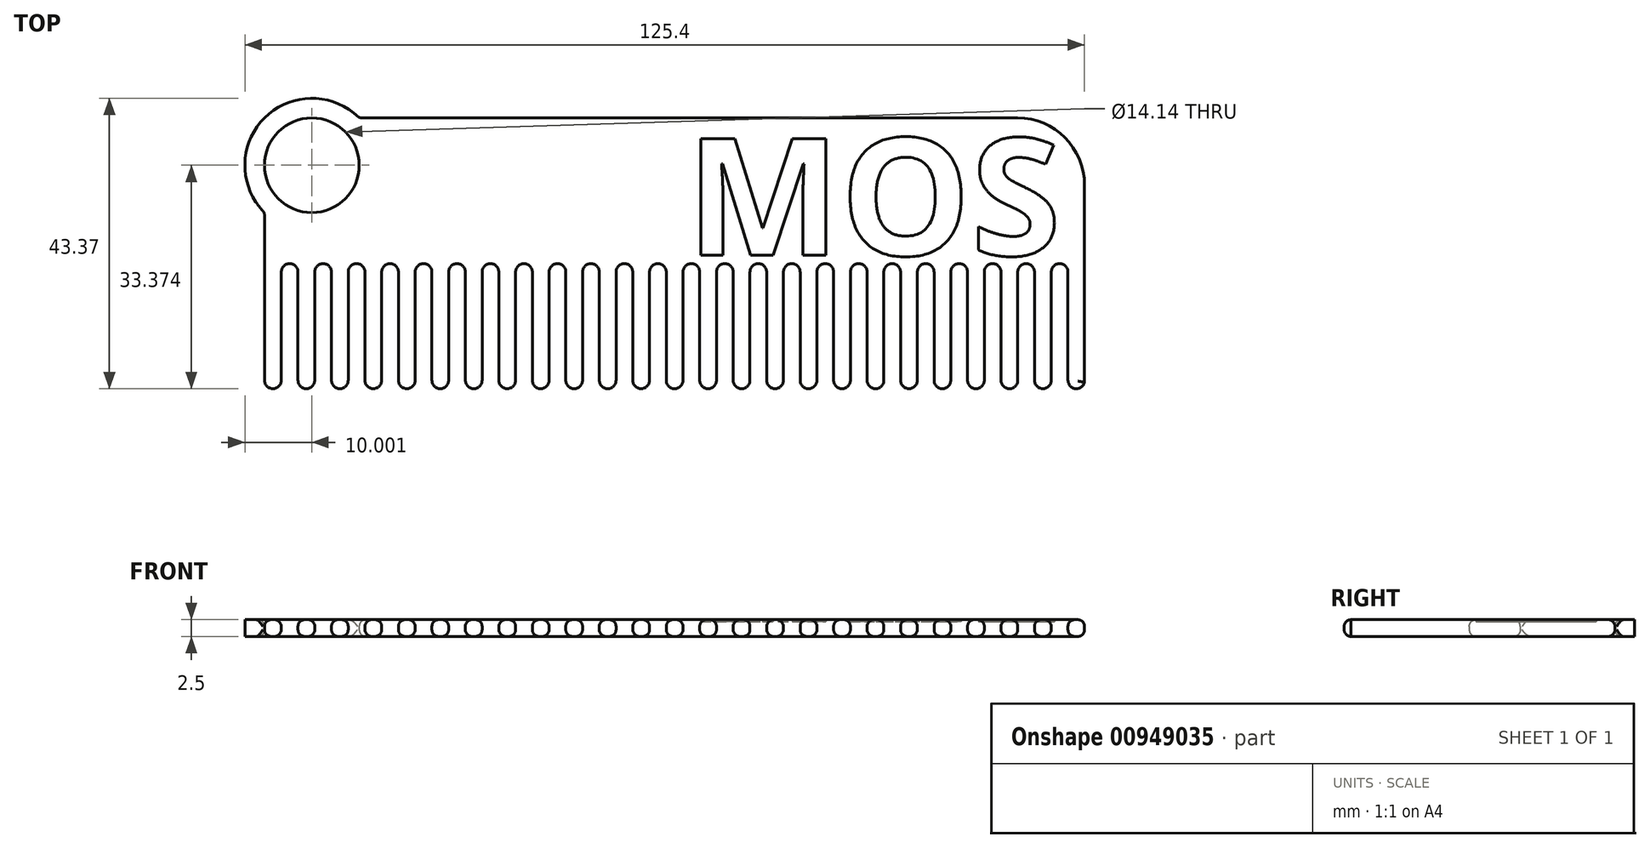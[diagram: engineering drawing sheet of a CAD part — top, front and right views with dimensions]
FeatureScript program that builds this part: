
annotation { "Feature Type Name" : "Feature", "Feature Type Description" : "" }
export const myFeature = defineFeature(function(context is Context, id is Id, definition is map)
    precondition{}
    {
        {
            var Q0;
            Q0=qCreatedBy(makeId("Top.planeOp"),FACE);
            var sketch = newSketch(context, id + "F0", { "sketchPlane" : qUnion([Q0])});
            skLineSegment(sketch, "E0.top", {"start": v(49.47, 20.52) * mm, "end": v(-63, 20.52) * mm});
            skLineSegment(sketch, "E0.left", {"start": v(59.47, -18.94) * mm, "end": v(59.47, 10.52) * mm});
            skLineSegment(sketch, "E1", {"start": v(-63, 20.52) * mm, "end": v(-55.93, 13.44) * mm, "construction": true});
            skCircle(sketch, "E2", {"center": v(-55.93, 13.44) * mm, "radius": 7.07 * mm});
            skCircle(sketch, "E3", {"center": v(-55.93, 13.44) * mm, "radius": 10 * mm});
            skPoint(sketch, "E4.visualSharp", {"position": v(59.47, 20.52) * mm});
            skArc(sketch, "E4.filletArc", {"start": v(59.47, 10.52) * mm, "mid": v(56.54, 17.59) * mm, "end": v(49.47, 20.52) * mm});
            skLineSegment(sketch, "E5", {"start": v(-63, -18.68) * mm, "end": v(-63, 20.52) * mm});
            skPoint(sketch, "E6", {"position": v(-60.5, -19.93) * mm});
            skPoint(sketch, "E7.1.0.0", {"position": v(-58, -19.93) * mm});
            skPoint(sketch, "E7.2.0.0", {"position": v(-55.5, -19.93) * mm});
            skPoint(sketch, "E7.3.0.0", {"position": v(-53, -19.93) * mm});
            skPoint(sketch, "E7.4.0.0", {"position": v(-50.5, -19.93) * mm});
            skPoint(sketch, "E7.5.0.0", {"position": v(-48, -19.93) * mm});
            skPoint(sketch, "E7.6.0.0", {"position": v(-45.5, -19.93) * mm});
            skPoint(sketch, "E7.7.0.0", {"position": v(-43, -19.93) * mm});
            skPoint(sketch, "E7.8.0.0", {"position": v(-40.5, -19.93) * mm});
            skPoint(sketch, "E7.9.0.0", {"position": v(-38, -19.93) * mm});
            skPoint(sketch, "E7.10.0.0", {"position": v(-35.5, -19.93) * mm});
            skPoint(sketch, "E7.11.0.0", {"position": v(-33, -19.93) * mm});
            skPoint(sketch, "E7.12.0.0", {"position": v(-30.5, -19.93) * mm});
            skPoint(sketch, "E7.13.0.0", {"position": v(-28, -19.93) * mm});
            skPoint(sketch, "E7.14.0.0", {"position": v(-25.5, -19.93) * mm});
            skPoint(sketch, "E7.15.0.0", {"position": v(-23, -19.93) * mm});
            skPoint(sketch, "E7.16.0.0", {"position": v(-20.5, -19.93) * mm});
            skPoint(sketch, "E7.17.0.0", {"position": v(-18, -19.93) * mm});
            skPoint(sketch, "E7.18.0.0", {"position": v(-15.5, -19.93) * mm});
            skPoint(sketch, "E7.19.0.0", {"position": v(-13, -19.93) * mm});
            skPoint(sketch, "E7.20.0.0", {"position": v(-10.5, -19.93) * mm});
            skPoint(sketch, "E7.21.0.0", {"position": v(-8, -19.93) * mm});
            skPoint(sketch, "E7.22.0.0", {"position": v(-5.5, -19.93) * mm});
            skPoint(sketch, "E7.23.0.0", {"position": v(-3, -19.93) * mm});
            skPoint(sketch, "E7.24.0.0", {"position": v(-0.5, -19.93) * mm});
            skPoint(sketch, "E7.25.0.0", {"position": v(2, -19.93) * mm});
            skPoint(sketch, "E7.26.0.0", {"position": v(4.5, -19.93) * mm});
            skPoint(sketch, "E7.27.0.0", {"position": v(7, -19.93) * mm});
            skPoint(sketch, "E7.28.0.0", {"position": v(9.5, -19.93) * mm});
            skPoint(sketch, "E7.29.0.0", {"position": v(12, -19.93) * mm});
            skPoint(sketch, "E7.30.0.0", {"position": v(14.5, -19.93) * mm});
            skPoint(sketch, "E7.31.0.0", {"position": v(17, -19.93) * mm});
            skPoint(sketch, "E7.32.0.0", {"position": v(19.5, -19.93) * mm});
            skPoint(sketch, "E7.33.0.0", {"position": v(22, -19.93) * mm});
            skPoint(sketch, "E7.34.0.0", {"position": v(24.5, -19.93) * mm});
            skPoint(sketch, "E7.35.0.0", {"position": v(27, -19.93) * mm});
            skPoint(sketch, "E7.36.0.0", {"position": v(29.5, -19.93) * mm});
            skPoint(sketch, "E7.37.0.0", {"position": v(32, -19.93) * mm});
            skPoint(sketch, "E7.38.0.0", {"position": v(34.5, -19.93) * mm});
            skPoint(sketch, "E7.39.0.0", {"position": v(37, -19.93) * mm});
            skPoint(sketch, "E7.40.0.0", {"position": v(39.5, -19.93) * mm});
            skPoint(sketch, "E7.41.0.0", {"position": v(42, -19.93) * mm});
            skPoint(sketch, "E7.42.0.0", {"position": v(44.5, -19.93) * mm});
            skPoint(sketch, "E7.43.0.0", {"position": v(47, -19.93) * mm});
            skPoint(sketch, "E7.44.0.0", {"position": v(49.5, -19.93) * mm});
            skPoint(sketch, "E7.45.0.0", {"position": v(52, -19.93) * mm});
            skPoint(sketch, "E7.46.0.0", {"position": v(54.5, -19.93) * mm});
            skPoint(sketch, "E7.47.0.0", {"position": v(57, -19.93) * mm});
            skLineSegment(sketch, "E8", {"start": v(57, -1.25) * mm, "end": v(-63, -1.25) * mm, "construction": true});
            skPoint(sketch, "E9", {"position": v(-60.5, -1.25) * mm});
            skPoint(sketch, "E10.1.0.0", {"position": v(-58, -1.25) * mm});
            skPoint(sketch, "E10.2.0.0", {"position": v(-55.5, -1.25) * mm});
            skPoint(sketch, "E10.3.0.0", {"position": v(-53, -1.25) * mm});
            skPoint(sketch, "E10.4.0.0", {"position": v(-50.5, -1.25) * mm});
            skPoint(sketch, "E10.5.0.0", {"position": v(-48, -1.25) * mm});
            skPoint(sketch, "E10.6.0.0", {"position": v(-45.5, -1.25) * mm});
            skPoint(sketch, "E10.7.0.0", {"position": v(-43, -1.25) * mm});
            skPoint(sketch, "E10.8.0.0", {"position": v(-40.5, -1.25) * mm});
            skPoint(sketch, "E10.9.0.0", {"position": v(-38, -1.25) * mm});
            skPoint(sketch, "E10.10.0.0", {"position": v(-35.5, -1.25) * mm});
            skPoint(sketch, "E10.11.0.0", {"position": v(-33, -1.25) * mm});
            skPoint(sketch, "E10.12.0.0", {"position": v(-30.5, -1.25) * mm});
            skPoint(sketch, "E10.13.0.0", {"position": v(-28, -1.25) * mm});
            skPoint(sketch, "E10.14.0.0", {"position": v(-25.5, -1.25) * mm});
            skPoint(sketch, "E10.15.0.0", {"position": v(-23, -1.25) * mm});
            skPoint(sketch, "E10.16.0.0", {"position": v(-20.5, -1.25) * mm});
            skPoint(sketch, "E10.17.0.0", {"position": v(-18, -1.25) * mm});
            skPoint(sketch, "E10.18.0.0", {"position": v(-15.5, -1.25) * mm});
            skPoint(sketch, "E10.19.0.0", {"position": v(-13, -1.25) * mm});
            skPoint(sketch, "E10.20.0.0", {"position": v(-10.5, -1.25) * mm});
            skPoint(sketch, "E10.21.0.0", {"position": v(-8, -1.25) * mm});
            skPoint(sketch, "E10.22.0.0", {"position": v(-5.5, -1.25) * mm});
            skPoint(sketch, "E10.23.0.0", {"position": v(-3, -1.25) * mm});
            skPoint(sketch, "E10.24.0.0", {"position": v(-0.5, -1.25) * mm});
            skPoint(sketch, "E10.25.0.0", {"position": v(2, -1.25) * mm});
            skPoint(sketch, "E10.26.0.0", {"position": v(4.5, -1.25) * mm});
            skPoint(sketch, "E10.27.0.0", {"position": v(7, -1.25) * mm});
            skPoint(sketch, "E10.28.0.0", {"position": v(9.5, -1.25) * mm});
            skPoint(sketch, "E10.29.0.0", {"position": v(12, -1.25) * mm});
            skPoint(sketch, "E10.30.0.0", {"position": v(14.5, -1.25) * mm});
            skPoint(sketch, "E10.31.0.0", {"position": v(17, -1.25) * mm});
            skPoint(sketch, "E10.32.0.0", {"position": v(19.5, -1.25) * mm});
            skPoint(sketch, "E10.33.0.0", {"position": v(22, -1.25) * mm});
            skPoint(sketch, "E10.34.0.0", {"position": v(24.5, -1.25) * mm});
            skPoint(sketch, "E10.35.0.0", {"position": v(27, -1.25) * mm});
            skPoint(sketch, "E10.36.0.0", {"position": v(29.5, -1.25) * mm});
            skPoint(sketch, "E10.37.0.0", {"position": v(32, -1.25) * mm});
            skPoint(sketch, "E10.38.0.0", {"position": v(34.5, -1.25) * mm});
            skPoint(sketch, "E10.39.0.0", {"position": v(37, -1.25) * mm});
            skPoint(sketch, "E10.40.0.0", {"position": v(39.5, -1.25) * mm});
            skPoint(sketch, "E10.41.0.0", {"position": v(42, -1.25) * mm});
            skPoint(sketch, "E10.42.0.0", {"position": v(44.5, -1.25) * mm});
            skPoint(sketch, "E10.43.0.0", {"position": v(47, -1.25) * mm});
            skPoint(sketch, "E10.44.0.0", {"position": v(49.5, -1.25) * mm});
            skPoint(sketch, "E10.45.0.0", {"position": v(52, -1.25) * mm});
            skPoint(sketch, "E10.46.0.0", {"position": v(54.5, -1.25) * mm});
            skPoint(sketch, "E10.47.0.0", {"position": v(57, -1.25) * mm});
            skLineSegment(sketch, "E10.direction1", {"start": v(-60.5, -1.25) * mm, "end": v(-58, -1.25) * mm, "construction": true});
            skPoint(sketch, "E11.positionSnap0", {"position": v(-59.25, -1.25) * mm});
            skArc(sketch, "E12", {"start": v(-58, -2.5) * mm, "mid": v(-59.25, -1.25) * mm, "end": v(-60.5, -2.5) * mm});
            skArc(sketch, "E13.1.0.0", {"start": v(-53, -2.5) * mm, "mid": v(-54.25, -1.25) * mm, "end": v(-55.5, -2.5) * mm});
            skArc(sketch, "E13.2.0.0", {"start": v(-48, -2.5) * mm, "mid": v(-49.25, -1.25) * mm, "end": v(-50.5, -2.5) * mm});
            skArc(sketch, "E13.3.0.0", {"start": v(-43, -2.5) * mm, "mid": v(-44.25, -1.25) * mm, "end": v(-45.5, -2.5) * mm});
            skArc(sketch, "E13.4.0.0", {"start": v(-38, -2.5) * mm, "mid": v(-39.25, -1.25) * mm, "end": v(-40.5, -2.5) * mm});
            skArc(sketch, "E13.5.0.0", {"start": v(-33, -2.5) * mm, "mid": v(-34.25, -1.25) * mm, "end": v(-35.5, -2.5) * mm});
            skArc(sketch, "E13.6.0.0", {"start": v(-28, -2.5) * mm, "mid": v(-29.25, -1.25) * mm, "end": v(-30.5, -2.5) * mm});
            skArc(sketch, "E13.7.0.0", {"start": v(-23, -2.5) * mm, "mid": v(-24.25, -1.25) * mm, "end": v(-25.5, -2.5) * mm});
            skArc(sketch, "E13.8.0.0", {"start": v(-18, -2.5) * mm, "mid": v(-19.25, -1.25) * mm, "end": v(-20.5, -2.5) * mm});
            skArc(sketch, "E13.9.0.0", {"start": v(-13, -2.5) * mm, "mid": v(-14.25, -1.25) * mm, "end": v(-15.5, -2.5) * mm});
            skArc(sketch, "E13.10.0.0", {"start": v(-8, -2.5) * mm, "mid": v(-9.25, -1.25) * mm, "end": v(-10.5, -2.5) * mm});
            skArc(sketch, "E13.11.0.0", {"start": v(-3, -2.5) * mm, "mid": v(-4.25, -1.25) * mm, "end": v(-5.5, -2.5) * mm});
            skArc(sketch, "E13.12.0.0", {"start": v(2, -2.5) * mm, "mid": v(0.75, -1.25) * mm, "end": v(-0.5, -2.5) * mm});
            skArc(sketch, "E13.13.0.0", {"start": v(7, -2.5) * mm, "mid": v(5.75, -1.25) * mm, "end": v(4.5, -2.5) * mm});
            skArc(sketch, "E13.14.0.0", {"start": v(12, -2.5) * mm, "mid": v(10.75, -1.25) * mm, "end": v(9.5, -2.5) * mm});
            skArc(sketch, "E13.15.0.0", {"start": v(17, -2.5) * mm, "mid": v(15.75, -1.25) * mm, "end": v(14.5, -2.5) * mm});
            skArc(sketch, "E13.16.0.0", {"start": v(22, -2.5) * mm, "mid": v(20.75, -1.25) * mm, "end": v(19.5, -2.5) * mm});
            skArc(sketch, "E13.17.0.0", {"start": v(27, -2.5) * mm, "mid": v(25.75, -1.25) * mm, "end": v(24.5, -2.5) * mm});
            skArc(sketch, "E13.18.0.0", {"start": v(32, -2.5) * mm, "mid": v(30.75, -1.25) * mm, "end": v(29.5, -2.5) * mm});
            skArc(sketch, "E13.19.0.0", {"start": v(37, -2.5) * mm, "mid": v(35.75, -1.25) * mm, "end": v(34.5, -2.5) * mm});
            skArc(sketch, "E13.20.0.0", {"start": v(42, -2.5) * mm, "mid": v(40.75, -1.25) * mm, "end": v(39.5, -2.5) * mm});
            skArc(sketch, "E13.21.0.0", {"start": v(47, -2.5) * mm, "mid": v(45.75, -1.25) * mm, "end": v(44.5, -2.5) * mm});
            skArc(sketch, "E13.22.0.0", {"start": v(52, -2.5) * mm, "mid": v(50.75, -1.25) * mm, "end": v(49.5, -2.5) * mm});
            skArc(sketch, "E13.23.0.0", {"start": v(57, -2.5) * mm, "mid": v(55.75, -1.25) * mm, "end": v(54.5, -2.5) * mm});
            skLineSegment(sketch, "E13.direction1", {"start": v(-59.25, -2.5) * mm, "end": v(-54.25, -2.5) * mm, "construction": true});
            skPoint(sketch, "E14.0.48.0", {"position": v(59.5, -1.25) * mm});
            skPoint(sketch, "E15.0.48.0", {"position": v(59.5, -19.93) * mm});
            skLineSegment(sketch, "E16", {"start": v(57, -1.25) * mm, "end": v(59.5, -1.25) * mm, "construction": true});
            skArc(sketch, "E17", {"start": v(-63, -18.68) * mm, "mid": v(-61.75, -19.93) * mm, "end": v(-60.5, -18.68) * mm});
            skArc(sketch, "E18.1.0.0", {"start": v(-58, -18.68) * mm, "mid": v(-56.75, -19.93) * mm, "end": v(-55.5, -18.68) * mm});
            skArc(sketch, "E18.2.0.0", {"start": v(-53, -18.68) * mm, "mid": v(-51.75, -19.93) * mm, "end": v(-50.5, -18.68) * mm});
            skArc(sketch, "E18.3.0.0", {"start": v(-48, -18.68) * mm, "mid": v(-46.75, -19.93) * mm, "end": v(-45.5, -18.68) * mm});
            skArc(sketch, "E18.4.0.0", {"start": v(-43, -18.68) * mm, "mid": v(-41.75, -19.93) * mm, "end": v(-40.5, -18.68) * mm});
            skArc(sketch, "E18.5.0.0", {"start": v(-38, -18.68) * mm, "mid": v(-36.75, -19.93) * mm, "end": v(-35.5, -18.68) * mm});
            skArc(sketch, "E18.6.0.0", {"start": v(-33, -18.68) * mm, "mid": v(-31.75, -19.93) * mm, "end": v(-30.5, -18.68) * mm});
            skArc(sketch, "E18.7.0.0", {"start": v(-28, -18.68) * mm, "mid": v(-26.75, -19.93) * mm, "end": v(-25.5, -18.68) * mm});
            skArc(sketch, "E18.8.0.0", {"start": v(-23, -18.68) * mm, "mid": v(-21.75, -19.93) * mm, "end": v(-20.5, -18.68) * mm});
            skArc(sketch, "E18.9.0.0", {"start": v(-18, -18.68) * mm, "mid": v(-16.75, -19.93) * mm, "end": v(-15.5, -18.68) * mm});
            skArc(sketch, "E18.10.0.0", {"start": v(-13, -18.68) * mm, "mid": v(-11.75, -19.93) * mm, "end": v(-10.5, -18.68) * mm});
            skArc(sketch, "E18.11.0.0", {"start": v(-8, -18.68) * mm, "mid": v(-6.75, -19.93) * mm, "end": v(-5.5, -18.68) * mm});
            skArc(sketch, "E18.12.0.0", {"start": v(-3, -18.68) * mm, "mid": v(-1.75, -19.93) * mm, "end": v(-0.5, -18.68) * mm});
            skArc(sketch, "E18.13.0.0", {"start": v(2, -18.68) * mm, "mid": v(3.25, -19.93) * mm, "end": v(4.5, -18.68) * mm});
            skArc(sketch, "E18.14.0.0", {"start": v(7, -18.68) * mm, "mid": v(8.25, -19.93) * mm, "end": v(9.5, -18.68) * mm});
            skArc(sketch, "E18.15.0.0", {"start": v(12, -18.68) * mm, "mid": v(13.25, -19.93) * mm, "end": v(14.5, -18.68) * mm});
            skArc(sketch, "E18.16.0.0", {"start": v(17, -18.68) * mm, "mid": v(18.25, -19.93) * mm, "end": v(19.5, -18.68) * mm});
            skArc(sketch, "E18.17.0.0", {"start": v(22, -18.68) * mm, "mid": v(23.25, -19.93) * mm, "end": v(24.5, -18.68) * mm});
            skArc(sketch, "E18.18.0.0", {"start": v(27, -18.68) * mm, "mid": v(28.25, -19.93) * mm, "end": v(29.5, -18.68) * mm});
            skArc(sketch, "E18.19.0.0", {"start": v(32, -18.68) * mm, "mid": v(33.25, -19.93) * mm, "end": v(34.5, -18.68) * mm});
            skArc(sketch, "E18.20.0.0", {"start": v(37, -18.68) * mm, "mid": v(38.25, -19.93) * mm, "end": v(39.5, -18.68) * mm});
            skArc(sketch, "E18.21.0.0", {"start": v(42, -18.68) * mm, "mid": v(43.25, -19.93) * mm, "end": v(44.5, -18.68) * mm});
            skArc(sketch, "E18.22.0.0", {"start": v(47, -18.68) * mm, "mid": v(48.25, -19.93) * mm, "end": v(49.5, -18.68) * mm});
            skArc(sketch, "E18.23.0.0", {"start": v(52, -18.68) * mm, "mid": v(53.25, -19.93) * mm, "end": v(54.5, -18.68) * mm});
            skLineSegment(sketch, "E18.direction1", {"start": v(-61.75, -18.68) * mm, "end": v(-56.75, -18.68) * mm, "construction": true});
            skArc(sketch, "E19.0.24.0", {"start": v(57, -18.68) * mm, "mid": v(58.12, -19.92) * mm, "end": v(59.47, -18.94) * mm});
            skLineSegment(sketch, "E20", {"start": v(-60.5, -1.25) * mm, "end": v(-60.5, -18.68) * mm});
            skLineSegment(sketch, "E21.1.0.0", {"start": v(-58, -1.25) * mm, "end": v(-58, -19.93) * mm});
            skLineSegment(sketch, "E21.2.0.0", {"start": v(-55.5, -1.25) * mm, "end": v(-55.5, -19.93) * mm});
            skLineSegment(sketch, "E21.3.0.0", {"start": v(-53, -1.25) * mm, "end": v(-53, -18.68) * mm});
            skLineSegment(sketch, "E21.4.0.0", {"start": v(-50.5, -1.25) * mm, "end": v(-50.5, -18.68) * mm});
            skLineSegment(sketch, "E21.5.0.0", {"start": v(-48, -1.25) * mm, "end": v(-48, -18.68) * mm});
            skLineSegment(sketch, "E21.6.0.0", {"start": v(-45.5, -1.25) * mm, "end": v(-45.5, -19.93) * mm});
            skLineSegment(sketch, "E21.7.0.0", {"start": v(-43, -1.25) * mm, "end": v(-43, -18.68) * mm});
            skLineSegment(sketch, "E21.8.0.0", {"start": v(-40.5, -1.25) * mm, "end": v(-40.5, -18.68) * mm});
            skLineSegment(sketch, "E21.9.0.0", {"start": v(-38, -1.25) * mm, "end": v(-38, -18.68) * mm});
            skLineSegment(sketch, "E21.10.0.0", {"start": v(-35.5, -1.25) * mm, "end": v(-35.5, -18.68) * mm});
            skLineSegment(sketch, "E21.11.0.0", {"start": v(-33, -1.25) * mm, "end": v(-33, -18.68) * mm});
            skLineSegment(sketch, "E21.12.0.0", {"start": v(-30.5, -1.25) * mm, "end": v(-30.5, -19.93) * mm});
            skLineSegment(sketch, "E21.13.0.0", {"start": v(-28, -1.25) * mm, "end": v(-28, -18.68) * mm});
            skLineSegment(sketch, "E21.14.0.0", {"start": v(-25.5, -1.25) * mm, "end": v(-25.5, -18.68) * mm});
            skLineSegment(sketch, "E21.15.0.0", {"start": v(-23, -1.25) * mm, "end": v(-23, -18.68) * mm});
            skLineSegment(sketch, "E21.16.0.0", {"start": v(-20.5, -1.25) * mm, "end": v(-20.5, -18.68) * mm});
            skLineSegment(sketch, "E21.17.0.0", {"start": v(-18, -1.25) * mm, "end": v(-18, -18.68) * mm});
            skLineSegment(sketch, "E21.18.0.0", {"start": v(-15.5, -1.25) * mm, "end": v(-15.5, -18.68) * mm});
            skLineSegment(sketch, "E21.19.0.0", {"start": v(-13, -1.25) * mm, "end": v(-13, -18.68) * mm});
            skLineSegment(sketch, "E21.20.0.0", {"start": v(-10.5, -1.25) * mm, "end": v(-10.5, -18.68) * mm});
            skLineSegment(sketch, "E21.21.0.0", {"start": v(-8, -1.25) * mm, "end": v(-8, -18.68) * mm});
            skLineSegment(sketch, "E21.22.0.0", {"start": v(-5.5, -1.25) * mm, "end": v(-5.5, -18.68) * mm});
            skLineSegment(sketch, "E21.23.0.0", {"start": v(-3, -1.25) * mm, "end": v(-3, -18.68) * mm});
            skLineSegment(sketch, "E21.24.0.0", {"start": v(-0.5, -1.25) * mm, "end": v(-0.5, -18.68) * mm});
            skLineSegment(sketch, "E21.25.0.0", {"start": v(2, -1.25) * mm, "end": v(2, -18.68) * mm});
            skLineSegment(sketch, "E21.26.0.0", {"start": v(4.5, -1.25) * mm, "end": v(4.5, -18.68) * mm});
            skLineSegment(sketch, "E21.27.0.0", {"start": v(7, -1.25) * mm, "end": v(7, -18.68) * mm});
            skLineSegment(sketch, "E21.28.0.0", {"start": v(9.5, -1.25) * mm, "end": v(9.5, -18.68) * mm});
            skLineSegment(sketch, "E21.29.0.0", {"start": v(12, -1.25) * mm, "end": v(12, -18.68) * mm});
            skLineSegment(sketch, "E21.30.0.0", {"start": v(14.5, -1.25) * mm, "end": v(14.5, -18.68) * mm});
            skLineSegment(sketch, "E21.31.0.0", {"start": v(17, -1.25) * mm, "end": v(17, -18.68) * mm});
            skLineSegment(sketch, "E21.32.0.0", {"start": v(19.5, -1.25) * mm, "end": v(19.5, -18.68) * mm});
            skLineSegment(sketch, "E21.33.0.0", {"start": v(22, -1.25) * mm, "end": v(22, -18.68) * mm});
            skLineSegment(sketch, "E21.34.0.0", {"start": v(24.5, -1.25) * mm, "end": v(24.5, -18.68) * mm});
            skLineSegment(sketch, "E21.35.0.0", {"start": v(27, -1.25) * mm, "end": v(27, -18.68) * mm});
            skLineSegment(sketch, "E21.36.0.0", {"start": v(29.5, -1.25) * mm, "end": v(29.5, -18.68) * mm});
            skLineSegment(sketch, "E21.37.0.0", {"start": v(32, -1.25) * mm, "end": v(32, -18.68) * mm});
            skLineSegment(sketch, "E21.38.0.0", {"start": v(34.5, -1.25) * mm, "end": v(34.5, -18.68) * mm});
            skLineSegment(sketch, "E21.39.0.0", {"start": v(37, -1.25) * mm, "end": v(37, -18.68) * mm});
            skLineSegment(sketch, "E21.40.0.0", {"start": v(39.5, -1.25) * mm, "end": v(39.5, -18.68) * mm});
            skLineSegment(sketch, "E21.41.0.0", {"start": v(42, -1.25) * mm, "end": v(42, -18.68) * mm});
            skLineSegment(sketch, "E21.42.0.0", {"start": v(44.5, -1.25) * mm, "end": v(44.5, -18.68) * mm});
            skLineSegment(sketch, "E21.43.0.0", {"start": v(47, -1.25) * mm, "end": v(47, -18.68) * mm});
            skLineSegment(sketch, "E21.44.0.0", {"start": v(49.5, -1.25) * mm, "end": v(49.5, -18.68) * mm});
            skLineSegment(sketch, "E21.45.0.0", {"start": v(52, -1.25) * mm, "end": v(52, -18.68) * mm});
            skLineSegment(sketch, "E21.46.0.0", {"start": v(54.5, -1.25) * mm, "end": v(54.5, -18.68) * mm});
            skLineSegment(sketch, "E21.47.0.0", {"start": v(57, -1.25) * mm, "end": v(57, -18.68) * mm});
            skPoint(sketch, "E22.orphan", {"position": v(-63, -19.93) * mm});
            skLineSegment(sketch, "E23.trimOffspring", {"start": v(-45.5, -19.93) * mm, "end": v(-46.75, -19.93) * mm});
            skText(sketch, "E24", { "text": "MOS", "fontName": "OpenSans-Bold.ttf"});
            skLineSegment(sketch, "E25", {"start": v(-63, -19.93) * mm, "end": v(59.5, -19.93) * mm, "construction": true});
            const initialGuessF0  = {"E24": [0, 0, 1, 0, 0.01759]};
            skSetInitialGuess(sketch, initialGuessF0);
            skSolve(sketch);
        }
        {
            var Q0;
            Q0=makeQuery(id+"F0.imprint","IMPRINT",FACE,{"disambiguationData":[TD([[makeQuery(id+"F0.imprint","IMPRINT",EDGE,{"derivedFrom":sQuery(id+"F0.wireOp",EDGE,"E0.left")}),1.0]])]});
            var Q1;
            {var subQ0=sQuery(id+"F0.wireOp",EDGE,"E3");var subQ1=sQuery(id+"F0.wireOp",EDGE,"E0.top");var subQ2=makeQuery(id+"F0.imprint","INTERSECT",VERTEX,{"derivedFrom":[subQ1,subQ0]});Q1=makeQuery(id+"F0.imprint","IMPRINT",FACE,{"disambiguationData":[TD([[makeQuery(id+"F0.imprint","IMPRINT",EDGE,{"disambiguationData":[TD([[subQ2,-1.0]])],"derivedFrom":subQ1}),1.0]])]});}
            var Q2;
            {var subQ0=sQuery(id+"F0.wireOp",EDGE,"E3");var subQ1=sQuery(id+"F0.wireOp",EDGE,"E0.top");var subQ2=makeQuery(id+"F0.imprint","INTERSECT",VERTEX,{"derivedFrom":[subQ1,subQ0]});Q2=makeQuery(id+"F0.imprint","IMPRINT",FACE,{"disambiguationData":[TD([[makeQuery(id+"F0.imprint","IMPRINT",EDGE,{"disambiguationData":[TD([[subQ2,-1.0]])],"derivedFrom":subQ1}),-1.0]])]});}
            var Q3;
            {var subQ1=sQuery(id+"F0.wireOp",EDGE,"E0.top");var subQ3=sQuery(id+"F0.wireOp",EDGE,"E2");var subQ4=makeQuery(id+"F0.imprint","INTERSECT",VERTEX,{"derivedFrom":[subQ1,subQ3]});Q3=makeQuery(id+"F0.imprint","IMPRINT",FACE,{"disambiguationData":[TD([[makeQuery(id+"F0.imprint","IMPRINT",EDGE,{"disambiguationData":[TD([[subQ4,-1.0]])],"derivedFrom":subQ3}),-1.0]])]});}
            var Q4;
            {var subQ0=sQuery(id+"F0.wireOp",EDGE,"E5");var subQ1=sQuery(id+"F0.wireOp",EDGE,"E3");var subQ3=makeQuery(id+"F0.imprint","INTERSECT",VERTEX,{"derivedFrom":[subQ1,subQ0]});Q4=makeQuery(id+"F0.imprint","IMPRINT",FACE,{"disambiguationData":[TD([[makeQuery(id+"F0.imprint","IMPRINT",EDGE,{"disambiguationData":[TD([[subQ3,-1.0]])],"derivedFrom":subQ0}),1.0]])]});}
            extrude(context, id + "F1", {"entities" : qUnion([Q0, Q1, Q2, Q3, Q4]), "depth" : 2.5 * mm, "offsetDistance" : 25 * mm});
        }
        {
            var Q0;
            Q0=makeQuery(id+"F0.imprint","IMPRINT",FACE,{"disambiguationData":[TD([[makeQuery(id+"F0.imprint","IMPRINT",EDGE,{"derivedFrom":sQuery(id+"F0.wireOp",EDGE,"E24.sketch_text.stroke-0")}),-1.0]])]});
            var Q1;
            Q1=makeQuery(id+"F0.imprint","IMPRINT",FACE,{"disambiguationData":[TD([[makeQuery(id+"F0.imprint","IMPRINT",EDGE,{"derivedFrom":sQuery(id+"F0.wireOp",EDGE,"E24.sketch_text.stroke-19")}),-1.0]])]});
            var Q2;
            Q2=makeQuery(id+"F0.imprint","IMPRINT",FACE,{"disambiguationData":[TD([[makeQuery(id+"F0.imprint","IMPRINT",EDGE,{"derivedFrom":sQuery(id+"F0.wireOp",EDGE,"E24.sketch_text.stroke-33")}),-1.0]])]});
            var Q3;
            Q3=makeQuery(id+"F0.imprint","IMPRINT",FACE,{"disambiguationData":[TD([[makeQuery(id+"F0.imprint","IMPRINT",EDGE,{"derivedFrom":sQuery(id+"F0.wireOp",EDGE,"E24.sketch_text.stroke-27")}),1.0]])]});
            extrude(context, id + "F2", {"entities" : qUnion([Q0, Q1, Q2, Q3]), "operationType" : NewBodyOperationType.ADD, "depth" : 2.2 * mm, "offsetDistance" : 25 * mm});
        }
        {
            var Q0;
            Q0=makeQuery(id+"F0.imprint","IMPRINT",FACE,{"disambiguationData":[TD([[makeQuery(id+"F0.imprint","IMPRINT",EDGE,{"derivedFrom":sQuery(id+"F0.wireOp",EDGE,"E24.sketch_text.stroke-27")}),1.0]])]});
            extrude(context, id + "F3", {"entities" : qUnion([Q0]), "operationType" : NewBodyOperationType.ADD, "depth" : 2.5 * mm, "offsetDistance" : 25 * mm});
        }
        {
            var Q0;
            Q0=makeQuery(id+"F1.opExtrude","SWEPT_FACE",FACE,{"disambiguationData":[OSD([sQuery(id+"F0.wireOp",EDGE,"E2")])]});
            var Q1;
            Q1=makeQuery(id+"F1.opExtrude","SWEPT_FACE",FACE,{"disambiguationData":[OSD([sQuery(id+"F0.wireOp",EDGE,"E0.top")])]});
            var Q2;
            Q2=makeQuery(id+"F1.opExtrude","SWEPT_FACE",FACE,{"disambiguationData":[OSD([sQuery(id+"F0.wireOp",EDGE,"E5")])]});
            fillet(context, id + "F4", {"entities" : qUnion([Q0, Q1, Q2]), "radius" : 1 * mm, "tangentPropagation" : true, "allowEdgeOverflow" : false});
        }
    });
